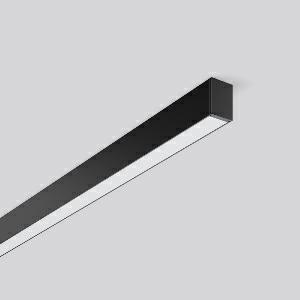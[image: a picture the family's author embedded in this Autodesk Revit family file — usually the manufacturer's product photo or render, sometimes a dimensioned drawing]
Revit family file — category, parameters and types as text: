
# Revit family: less_is_more_27_312196_003_1_e3b7
name_source: partatom
category: Lighting Fixtures
units: mm (PartAtom-declared; Revit-internal decimal feet)

## family parameters
Cut with Voids When Loaded = No
Host = Face
Light Source = No
Part Type = Normal
Room Calculation Point = No
Round Connector Dimension = Use Diameter
Shared = No

## types (1)
- LESS IS MORE 27 (1 x LED Modul 840, 1600 lm, 4000)
    Apparent Load = 25 VA
    CIE Flux Codes = 48 79 96 100 100
    Color Rendering = 80
    Color Temperature = 4000
    Default Elevation = 1800 mm
    Description = Series: LESS IS MORE 27
Ceiling and wall luminaire with slim design. Housing: extruded aluminium profile, powder-coated. End cap aluminium powder-coated. Diffuser made of non-yellowing plastic (PMMA), opal. Suitable for Ceiling mounting, Wall (surface). External driver with connecting cable. 
Colour: deep black, matt (RAL 9005)
Length: 1012 mm
Width: 28 mm
Height: 38 mm
Lamp: LED
Socket: without socket
Colour temperature: 4000K
Colour rendering index (CRI): 82
System power: 25 W
Rated luminous flux: 1600 lm
Luminous efficiency: 64 lm/W
Control gear: Regulated power supply
Protection class: II
Type of protection: IP 20
    Height = 38 mm
    Lamp = 1 x LED Modul 840
    Lamp Light Flux = 1600 lm
    Lamp count = 1
    Length = 1012 mm
    Lifetime = 50000 h
    Luminous efficacy = 64 lm/W
    Manufacturer = RZB
    ModVariant = No
    Model = 312196.003.1
    Mounting Place = Ceiling, Wall
    Mounting Type = Surface mounted
    Number of Poles = 1
    OnlyDefault = Yes
    Power Factor = 1
    Product Name = LESS IS MORE 27
    Product group = Surface mounted LED linear luminaires
    ProductGroupID = 307
    Protection Class = Protection class II
    Protection Degree = IP 20
    RLX_Detail_Level = 1
    RLX_Emergency_Light_Flux = 0 lm
    RLX_Emergency_Type = 0
    RLX_Emergency_Type_DB = No
    RlxData = <blob elided: 28637 chars, md5=2e36f925>
    Socket = socket
    Standby Power = 0 W
    System Light Flux = 1600 lm
    System Power = 25 W
    Type Comments = Product without accessories
    Type Image = 312196.003.jpg
    URL = http://relux.com
    VarID = ---
    Voltage = 230 V
    Voltage Range = 220-240 V
    Weight = 0.00 kg
    Width = 28 mm

## geometry (parser evidence)
native form markers: Blend x4, Sweep x11
no freeform markers — native parametric forms only
